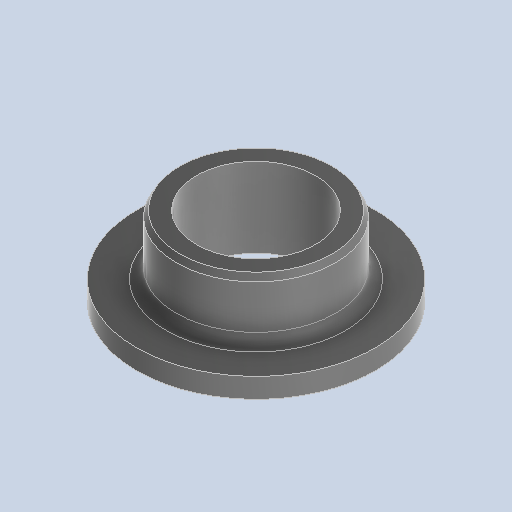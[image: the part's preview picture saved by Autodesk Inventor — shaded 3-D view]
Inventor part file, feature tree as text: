
AUTODESK INVENTOR PART (.ipt)
format: ipt  version: 2024.2 (Build 282272000, 272)  size: 269,824 bytes
history: native  units: mm
features: revolve x1, fillet x1, sketch x1
ambient origin geometry x8: Origin, YZ Plane, XZ Plane, XY Plane, X Axis, Y Axis, Z Axis, Center Point
bodies: Solid1 (feature_tree)
feature tree (3):
  revolve  "Revolution1"  Angle=30.0deg
  fillet  "Fillet1"  Radius=0.5mm
  sketch  "Sketch1"  dims[d5=90.0deg d11=30.0deg d12=0.5mm]
